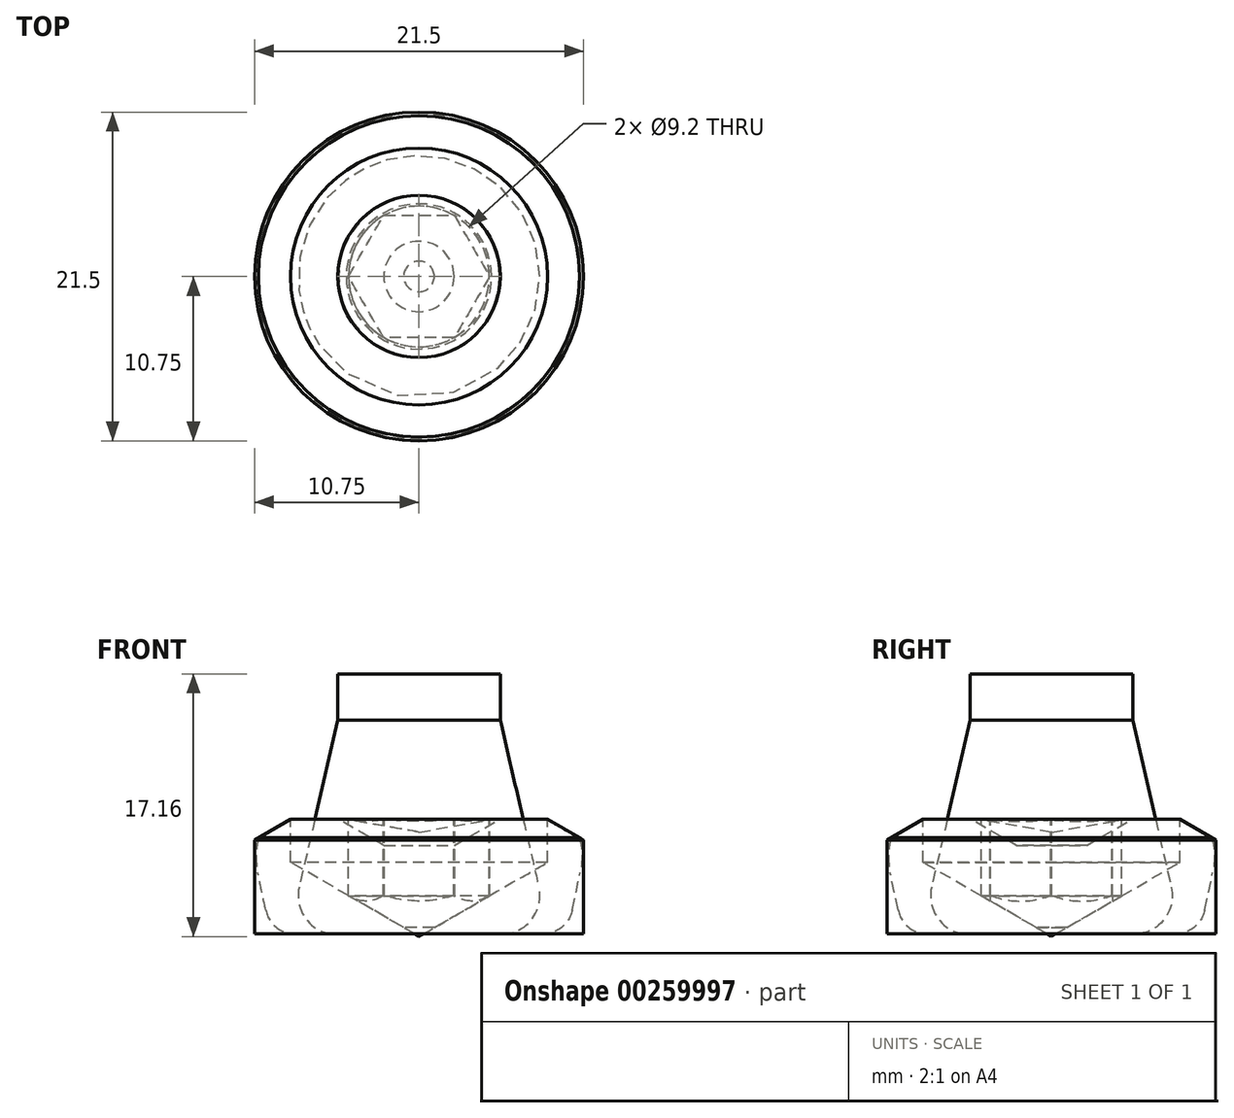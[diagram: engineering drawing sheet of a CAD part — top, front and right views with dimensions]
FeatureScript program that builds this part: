
annotation { "Feature Type Name" : "Feature", "Feature Type Description" : "" }
export const myFeature = defineFeature(function(context is Context, id is Id, definition is map)
    precondition{}
    {
        {
            var Q0;
            Q0=qCreatedBy(makeId("Front.planeOp"),FACE);
            var sketch = newSketch(context, id + "F0", { "sketchPlane" : qUnion([Q0])});
            skLineSegment(sketch, "E0", {"start": v(0, 0) * mm, "end": v(0, 17) * mm, "construction": true});
            skLineSegment(sketch, "E1", {"start": v(0, 17) * mm, "end": v(5.3, 17) * mm});
            skLineSegment(sketch, "E2", {"start": v(5.3, 17) * mm, "end": v(5.3, 14) * mm});
            skLineSegment(sketch, "E3", {"start": v(5.3, 14) * mm, "end": v(7.84, 3.06) * mm});
            skLineSegment(sketch, "E4", {"start": v(5.4, 0) * mm, "end": v(0, 0) * mm});
            skLineSegment(sketch, "E5", {"start": v(0, 17) * mm, "end": v(0, 0) * mm});
            skPoint(sketch, "E6.visualSharp", {"position": v(8.54, 0) * mm});
            skArc(sketch, "E6.filletArc", {"start": v(5.4, 0) * mm, "mid": v(7.36, 0.94) * mm, "end": v(7.84, 3.06) * mm});
            skSolve(sketch);
        }
        {
            var Q0;
            Q0=qSketchRegion(id+"F0",true);
            var Q1;
            Q1=sQuery(id+"F0.wireOp",EDGE,"E5");
            revolve(context, id + "F1", {"entities" : qUnion([Q0]), "axis" : qUnion([Q1]), "revolveType" : RevolveType.FULL});
        }
        {
            var Q0;
            Q0=qCreatedBy(makeId("Front.planeOp"),FACE);
            var sketch = newSketch(context, id + "F2", { "sketchPlane" : qUnion([Q0])});
            skLineSegment(sketch, "E7", {"start": v(0, 0) * mm, "end": v(0, 5.8) * mm});
            skLineSegment(sketch, "E8", {"start": v(10.54, 4.02) * mm, "end": v(10.02, 1.58) * mm});
            skLineSegment(sketch, "E9", {"start": v(8.07, 0) * mm, "end": v(0, 0) * mm});
            skLineSegment(sketch, "E10", {"start": v(0, 5.8) * mm, "end": v(0, 0) * mm, "construction": true});
            skLineSegment(sketch, "E11", {"start": v(0, 5.8) * mm, "end": v(2.3, 5.8) * mm});
            skLineSegment(sketch, "E12", {"start": v(2.3, 5.8) * mm, "end": v(5.25, 7.5) * mm});
            skLineSegment(sketch, "E13", {"start": v(5.25, 7.5) * mm, "end": v(8.4, 7.5) * mm});
            skArc(sketch, "E14.filletArc", {"start": v(10.54, 4.02) * mm, "mid": v(10.65, 5.16) * mm, "end": v(10.5, 6.29) * mm});
            skLineSegment(sketch, "E15", {"start": v(10.54, 4.02) * mm, "end": v(10.75, 5) * mm, "construction": true});
            skLineSegment(sketch, "E16", {"start": v(8.4, 7.5) * mm, "end": v(10.5, 6.29) * mm});
            skPoint(sketch, "E17.visualSharp", {"position": v(9.69, 0) * mm});
            skArc(sketch, "E17.filletArc", {"start": v(8.07, 0) * mm, "mid": v(9.33, 0.45) * mm, "end": v(10.02, 1.58) * mm});
            skSolve(sketch);
        }
        {
            var Q0;
            Q0=qSketchRegion(id+"F2",true);
            var Q1;
            Q1=sQuery(id+"F2.wireOp",EDGE,"E7");
            revolve(context, id + "F3", {"entities" : qUnion([Q0]), "axis" : qUnion([Q1]), "revolveType" : RevolveType.FULL});
        }
        {
            var Q0;
            Q0=qCreatedBy(makeId("Front.planeOp"),FACE);
            var sketch = newSketch(context, id + "F4", { "sketchPlane" : qUnion([Q0])});
            skLineSegment(sketch, "E18", {"start": v(0, 0) * mm, "end": v(0, 0.42) * mm, "construction": true});
            skLineSegment(sketch, "E19", {"start": v(4.6, 7.5) * mm, "end": v(8.4, 7.5) * mm});
            skLineSegment(sketch, "E20", {"start": v(10.75, 6.14) * mm, "end": v(10.75, 0) * mm});
            skLineSegment(sketch, "E21", {"start": v(10.75, 0) * mm, "end": v(0, 0) * mm});
            skPoint(sketch, "E22.visualSharp", {"position": v(10.75, 7.5) * mm});
            skLineSegment(sketch, "E23", {"start": v(4.6, 7.5) * mm, "end": v(4.6, 2.5) * mm});
            skLineSegment(sketch, "E24", {"start": v(4.6, 2.5) * mm, "end": v(1, 0.42) * mm});
            skLineSegment(sketch, "E25", {"start": v(1, 0.42) * mm, "end": v(0, 0.42) * mm});
            skLineSegment(sketch, "E26", {"start": v(0, 0.42) * mm, "end": v(0, 0) * mm});
            skLineSegment(sketch, "E27", {"start": v(8.4, 7.5) * mm, "end": v(10.75, 6.14) * mm});
            skSolve(sketch);
        }
        {
            var Q0;
            Q0=qSketchRegion(id+"F4",true);
            var Q1;
            Q1=sQuery(id+"F4.wireOp",EDGE,"E26");
            revolve(context, id + "F5", {"entities" : qUnion([Q0]), "axis" : qUnion([Q1]), "revolveType" : RevolveType.FULL});
        }
        {
            var Q0;
            Q0=makeQuery(id+"F5.opRevolve","SWEPT_FACE",FACE,{"disambiguationData":[OSD([sQuery(id+"F4.wireOp",EDGE,"E19")])]});
            var sketch = newSketch(context, id + "F6", { "sketchPlane" : qUnion([Q0])});
            skCircle(sketch, "E28", {"center": v(0, 0) * mm, "radius": 4.6 * mm});
            skCircle(sketch, "E29.cCircle", {"center": v(0, 0) * mm, "radius": 4 * mm, "construction": true});
            skLineSegment(sketch, "E29.0", {"start": v(-2.3, 4) * mm, "end": v(2.3, 4) * mm});
            skLineSegment(sketch, "E29.1", {"start": v(2.3, 4) * mm, "end": v(4.62, 0) * mm});
            skLineSegment(sketch, "E29.2", {"start": v(4.62, 0) * mm, "end": v(2.3, -4) * mm});
            skLineSegment(sketch, "E29.3", {"start": v(2.3, -4) * mm, "end": v(-2.3, -4) * mm});
            skLineSegment(sketch, "E29.4", {"start": v(-2.3, -4) * mm, "end": v(-4.62, 0) * mm});
            skLineSegment(sketch, "E29.5", {"start": v(-4.62, 0) * mm, "end": v(-2.3, 4) * mm});
            skPoint(sketch, "E29.0.midPoint", {"position": v(0, 4) * mm});
            skSolve(sketch);
        }
        {
            var Q0;
            {var subQ0=sQuery(id+"F6.wireOp",EDGE,"E29.1");var subQ1=sQuery(id+"F6.wireOp",EDGE,"E28");var subQ2=makeQuery(id+"F6.imprint","INTERSECT",VERTEX,{"disambiguationData":[OD(0.0)],"derivedFrom":[subQ1,subQ0]});Q0=makeQuery(id+"F6.imprint","IMPRINT",FACE,{"disambiguationData":[TD([[makeQuery(id+"F6.imprint","IMPRINT",EDGE,{"disambiguationData":[TD([[subQ2,1.0]])],"derivedFrom":subQ1}),1.0]])]});}
            var Q1;
            {var subQ0=sQuery(id+"F6.wireOp",EDGE,"E29.1");var subQ1=sQuery(id+"F6.wireOp",EDGE,"E28");var subQ2=makeQuery(id+"F6.imprint","INTERSECT",VERTEX,{"disambiguationData":[OD(0.0)],"derivedFrom":[subQ1,subQ0]});Q1=makeQuery(id+"F6.imprint","IMPRINT",FACE,{"disambiguationData":[TD([[makeQuery(id+"F6.imprint","IMPRINT",EDGE,{"disambiguationData":[TD([[subQ2,-1.0]])],"derivedFrom":subQ1}),-1.0]])]});}
            var Q2;
            {var subQ0=sQuery(id+"F6.wireOp",EDGE,"E29.0");var subQ1=sQuery(id+"F6.wireOp",EDGE,"E28");var subQ2=makeQuery(id+"F6.imprint","INTERSECT",VERTEX,{"disambiguationData":[OD(0.0)],"derivedFrom":[subQ1,subQ0]});Q2=makeQuery(id+"F6.imprint","IMPRINT",FACE,{"disambiguationData":[TD([[makeQuery(id+"F6.imprint","IMPRINT",EDGE,{"disambiguationData":[TD([[subQ2,-1.0]])],"derivedFrom":subQ1}),1.0]])]});}
            var Q3;
            {var subQ0=sQuery(id+"F6.wireOp",EDGE,"E29.0");var subQ1=sQuery(id+"F6.wireOp",EDGE,"E28");var subQ2=makeQuery(id+"F6.imprint","INTERSECT",VERTEX,{"disambiguationData":[OD(1.0)],"derivedFrom":[subQ1,subQ0]});Q3=makeQuery(id+"F6.imprint","IMPRINT",FACE,{"disambiguationData":[TD([[makeQuery(id+"F6.imprint","IMPRINT",EDGE,{"disambiguationData":[TD([[subQ2,-1.0]])],"derivedFrom":subQ1}),-1.0]])]});}
            var Q4;
            {var subQ0=sQuery(id+"F6.wireOp",EDGE,"E29.5");var subQ1=sQuery(id+"F6.wireOp",EDGE,"E28");var subQ2=makeQuery(id+"F6.imprint","INTERSECT",VERTEX,{"disambiguationData":[OD(0.0)],"derivedFrom":[subQ1,subQ0]});Q4=makeQuery(id+"F6.imprint","IMPRINT",FACE,{"disambiguationData":[TD([[makeQuery(id+"F6.imprint","IMPRINT",EDGE,{"disambiguationData":[TD([[subQ2,-1.0]])],"derivedFrom":subQ1}),1.0]])]});}
            var Q5;
            {var subQ0=sQuery(id+"F6.wireOp",EDGE,"E29.5");var subQ1=sQuery(id+"F6.wireOp",EDGE,"E28");var subQ2=makeQuery(id+"F6.imprint","INTERSECT",VERTEX,{"disambiguationData":[OD(1.0)],"derivedFrom":[subQ1,subQ0]});Q5=makeQuery(id+"F6.imprint","IMPRINT",FACE,{"disambiguationData":[TD([[makeQuery(id+"F6.imprint","IMPRINT",EDGE,{"disambiguationData":[TD([[subQ2,-1.0]])],"derivedFrom":subQ1}),-1.0]])]});}
            var Q6;
            {var subQ0=sQuery(id+"F6.wireOp",EDGE,"E29.4");var subQ1=sQuery(id+"F6.wireOp",EDGE,"E28");var subQ2=makeQuery(id+"F6.imprint","INTERSECT",VERTEX,{"disambiguationData":[OD(0.0)],"derivedFrom":[subQ1,subQ0]});Q6=makeQuery(id+"F6.imprint","IMPRINT",FACE,{"disambiguationData":[TD([[makeQuery(id+"F6.imprint","IMPRINT",EDGE,{"disambiguationData":[TD([[subQ2,-1.0]])],"derivedFrom":subQ1}),1.0]])]});}
            var Q7;
            {var subQ0=sQuery(id+"F6.wireOp",EDGE,"E29.4");var subQ1=sQuery(id+"F6.wireOp",EDGE,"E28");var subQ2=makeQuery(id+"F6.imprint","INTERSECT",VERTEX,{"disambiguationData":[OD(1.0)],"derivedFrom":[subQ1,subQ0]});Q7=makeQuery(id+"F6.imprint","IMPRINT",FACE,{"disambiguationData":[TD([[makeQuery(id+"F6.imprint","IMPRINT",EDGE,{"disambiguationData":[TD([[subQ2,-1.0]])],"derivedFrom":subQ1}),-1.0]])]});}
            var Q8;
            {var subQ0=sQuery(id+"F6.wireOp",EDGE,"E29.3");var subQ1=sQuery(id+"F6.wireOp",EDGE,"E28");var subQ2=makeQuery(id+"F6.imprint","INTERSECT",VERTEX,{"disambiguationData":[OD(0.0)],"derivedFrom":[subQ1,subQ0]});Q8=makeQuery(id+"F6.imprint","IMPRINT",FACE,{"disambiguationData":[TD([[makeQuery(id+"F6.imprint","IMPRINT",EDGE,{"disambiguationData":[TD([[subQ2,-1.0]])],"derivedFrom":subQ1}),1.0]])]});}
            var Q9;
            {var subQ0=sQuery(id+"F6.wireOp",EDGE,"E29.3");var subQ1=sQuery(id+"F6.wireOp",EDGE,"E28");var subQ2=makeQuery(id+"F6.imprint","INTERSECT",VERTEX,{"disambiguationData":[OD(1.0)],"derivedFrom":[subQ1,subQ0]});Q9=makeQuery(id+"F6.imprint","IMPRINT",FACE,{"disambiguationData":[TD([[makeQuery(id+"F6.imprint","IMPRINT",EDGE,{"disambiguationData":[TD([[subQ2,-1.0]])],"derivedFrom":subQ1}),-1.0]])]});}
            var Q10;
            {var subQ0=sQuery(id+"F6.wireOp",EDGE,"E29.2");var subQ1=sQuery(id+"F6.wireOp",EDGE,"E28");var subQ2=makeQuery(id+"F6.imprint","INTERSECT",VERTEX,{"disambiguationData":[OD(0.0)],"derivedFrom":[subQ1,subQ0]});Q10=makeQuery(id+"F6.imprint","IMPRINT",FACE,{"disambiguationData":[TD([[makeQuery(id+"F6.imprint","IMPRINT",EDGE,{"disambiguationData":[TD([[subQ2,-1.0]])],"derivedFrom":subQ1}),1.0]])]});}
            var Q11;
            {var subQ0=sQuery(id+"F6.wireOp",EDGE,"E29.1");var subQ1=sQuery(id+"F6.wireOp",EDGE,"E28");var subQ2=makeQuery(id+"F6.imprint","INTERSECT",VERTEX,{"disambiguationData":[OD(1.0)],"derivedFrom":[subQ1,subQ0]});Q11=makeQuery(id+"F6.imprint","IMPRINT",FACE,{"disambiguationData":[TD([[makeQuery(id+"F6.imprint","IMPRINT",EDGE,{"disambiguationData":[TD([[subQ2,1.0]])],"derivedFrom":subQ1}),-1.0]])]});}
            var Q12;
            Q12=makeQuery(id+"F5.opRevolve","SWEPT_FACE",FACE,{"disambiguationData":[OSD([sQuery(id+"F4.wireOp",EDGE,"E24")])]});
            extrude(context, id + "F7", {"entities" : qUnion([Q0, Q1, Q2, Q3, Q4, Q5, Q6, Q7, Q8, Q9, Q10, Q11]), "operationType" : NewBodyOperationType.ADD, "endBound" : BoundingType.UP_TO_SURFACE, "oppositeDirection" : true, "endBoundEntityFace" : qUnion([Q12]), "depth" : 25 * mm});
        }
        {
            var Q0;
            Q0=makeQuery(id+"F7.boolean.opBoolean","MERGE",FACE,{"derivedFrom":[makeQuery(id+"F5.opRevolve","SWEPT_FACE",FACE,{"disambiguationData":[OSD([sQuery(id+"F4.wireOp",EDGE,"E19")])]}),makeQuery(id+"F7.opExtrude","CAP_FACE",FACE,{"disambiguationData":[OSD([sQuery(id+"F6.wireOp",EDGE,"axiUSiGf-8ymJ-Ezfh-tHsk-ULXXzRlxOoBz"),sQuery(id+"F6.wireOp",EDGE,"WrdyBTnM-XU54-uk96-2Sjo-h1HHDxb1zyqn"),sQuery(id+"F6.wireOp",EDGE,"7iNK7enz-fUzD-7EQp-KRCh-aPKnPlRcPdaK"),sQuery(id+"F6.wireOp",EDGE,"e7c95674-c634-4135-8625-61586754ee6a.1.0"),sQuery(id+"F6.wireOp",EDGE,"e7c95674-c634-4135-8625-61586754ee6a.1.1"),sQuery(id+"F6.wireOp",EDGE,"e7c95674-c634-4135-8625-61586754ee6a.1.2"),sQuery(id+"F6.wireOp",EDGE,"e7c95674-c634-4135-8625-61586754ee6a.2.0"),sQuery(id+"F6.wireOp",EDGE,"e7c95674-c634-4135-8625-61586754ee6a.2.1"),sQuery(id+"F6.wireOp",EDGE,"e7c95674-c634-4135-8625-61586754ee6a.2.2"),sQuery(id+"F6.wireOp",EDGE,"e7c95674-c634-4135-8625-61586754ee6a.3.0"),sQuery(id+"F6.wireOp",EDGE,"e7c95674-c634-4135-8625-61586754ee6a.3.1"),sQuery(id+"F6.wireOp",EDGE,"e7c95674-c634-4135-8625-61586754ee6a.3.2"),sQuery(id+"F6.wireOp",EDGE,"e7c95674-c634-4135-8625-61586754ee6a.4.0"),sQuery(id+"F6.wireOp",EDGE,"e7c95674-c634-4135-8625-61586754ee6a.4.1"),sQuery(id+"F6.wireOp",EDGE,"e7c95674-c634-4135-8625-61586754ee6a.4.2"),sQuery(id+"F6.wireOp",EDGE,"e7c95674-c634-4135-8625-61586754ee6a.5.0"),sQuery(id+"F6.wireOp",EDGE,"e7c95674-c634-4135-8625-61586754ee6a.5.1"),sQuery(id+"F6.wireOp",EDGE,"e7c95674-c634-4135-8625-61586754ee6a.5.2"),sQuery(id+"F6.wireOp",EDGE,"c34f7dbc-1fd9-48ae-9599-0fb72b0d65de.filletArc"),sQuery(id+"F6.wireOp",EDGE,"5fecc0f4-c57f-42b8-a97f-f8fbf54cf4db.filletArc"),sQuery(id+"F6.wireOp",EDGE,"b077568f-b672-48a6-a184-fa18c1575088.filletArc"),sQuery(id+"F6.wireOp",EDGE,"4c4ba650-eb3b-40a6-a5b6-7d0bcd232093.filletArc"),sQuery(id+"F6.wireOp",EDGE,"b016cc09-0b8d-437b-9508-1d7630c9d4ff.filletArc"),sQuery(id+"F6.wireOp",EDGE,"d5479cb3-145b-41e2-b586-5ab3f6452500.filletArc"),sQuery(id+"F6.wireOp",EDGE,"E28")])],"isStart":true})]});
            var sketch = newSketch(context, id + "F8", { "sketchPlane" : qUnion([Q0])});
            skCircle(sketch, "E30", {"center": v(0, 0) * mm, "radius": 4.75 * mm});
            skSolve(sketch);
        }
        {
            var Q0;
            Q0=qSketchRegion(id+"F8",true);
            extrude(context, id + "F9", {"entities" : qUnion([Q0]), "operationType" : NewBodyOperationType.REMOVE, "oppositeDirection" : true, "depth" : 1 * mm, "hasDraft" : true, "draftAngle" : 80 * degree, "draftPullDirection" : true});
        }
    });
